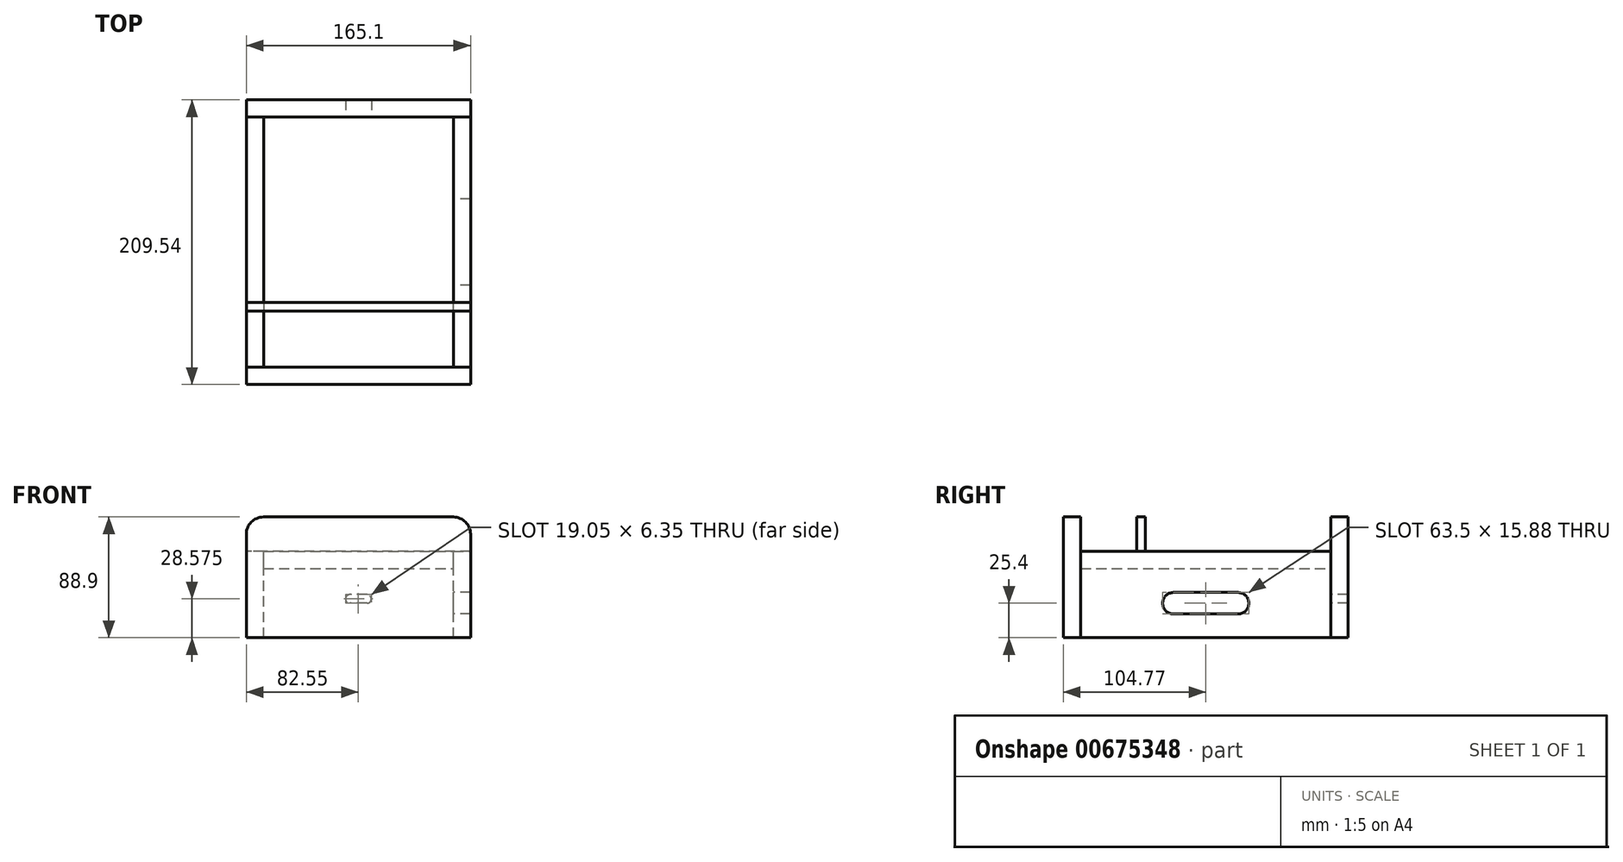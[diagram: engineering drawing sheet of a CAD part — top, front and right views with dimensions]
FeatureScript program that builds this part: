
annotation { "Feature Type Name" : "Feature", "Feature Type Description" : "" }
export const myFeature = defineFeature(function(context is Context, id is Id, definition is map)
    precondition{}
    {
        {
            var Q0;
            Q0=qCreatedBy(makeId("Top.planeOp"),FACE);
            var sketch = newSketch(context, id + "F0", { "sketchPlane" : qUnion([Q0])});
            skLineSegment(sketch, "E0.bottom", {"start": v(69.85, -92.07) * mm, "end": v(-69.85, -92.08) * mm, "construction": true});
            skLineSegment(sketch, "E0.top", {"start": v(69.85, 92.08) * mm, "end": v(-69.85, 92.07) * mm, "construction": true});
            skLineSegment(sketch, "E0.left", {"start": v(69.85, -92.07) * mm, "end": v(69.85, 92.08) * mm, "construction": true});
            skLineSegment(sketch, "E0.right", {"start": v(-69.85, -92.08) * mm, "end": v(-69.85, 92.07) * mm, "construction": true});
            skPoint(sketch, "E0.middle", {"position": v(0, 0) * mm});
            skLineSegment(sketch, "E1.bottom", {"start": v(-69.85, -92.08) * mm, "end": v(-82.55, -92.08) * mm});
            skLineSegment(sketch, "E1.top", {"start": v(-69.85, 92.07) * mm, "end": v(-82.55, 92.07) * mm});
            skLineSegment(sketch, "E1.left", {"start": v(-69.85, -92.08) * mm, "end": v(-69.85, 92.07) * mm});
            skLineSegment(sketch, "E1.right", {"start": v(-82.55, -92.08) * mm, "end": v(-82.55, 92.07) * mm});
            skLineSegment(sketch, "E2.bottom", {"start": v(69.85, -92.07) * mm, "end": v(82.55, -92.07) * mm});
            skLineSegment(sketch, "E2.top", {"start": v(69.85, 92.08) * mm, "end": v(82.55, 92.08) * mm});
            skLineSegment(sketch, "E2.left", {"start": v(69.85, -92.07) * mm, "end": v(69.85, 92.08) * mm});
            skLineSegment(sketch, "E2.right", {"start": v(82.55, -92.07) * mm, "end": v(82.55, 92.08) * mm});
            skLineSegment(sketch, "E3.bottom", {"start": v(82.55, 92.08) * mm, "end": v(-82.55, 92.07) * mm});
            skLineSegment(sketch, "E3.top", {"start": v(82.55, 104.78) * mm, "end": v(-82.55, 104.77) * mm});
            skLineSegment(sketch, "E3.left", {"start": v(82.55, 92.08) * mm, "end": v(82.55, 104.78) * mm});
            skLineSegment(sketch, "E3.right", {"start": v(-82.55, 92.07) * mm, "end": v(-82.55, 104.77) * mm});
            skLineSegment(sketch, "E4.bottom", {"start": v(-82.55, -92.08) * mm, "end": v(82.55, -92.08) * mm});
            skLineSegment(sketch, "E4.top", {"start": v(-82.55, -104.78) * mm, "end": v(82.55, -104.78) * mm});
            skLineSegment(sketch, "E4.left", {"start": v(-82.55, -92.08) * mm, "end": v(-82.55, -104.78) * mm});
            skLineSegment(sketch, "E4.right", {"start": v(82.55, -92.07) * mm, "end": v(82.55, -104.78) * mm});
            skSolve(sketch);
        }
        {
            var Q0;
            {var subQ0=sQuery(id+"F0.wireOp",EDGE,"E2.left");Q0=makeQuery(id+"F0.imprint","IMPRINT",FACE,{"disambiguationData":[TD([[makeQuery(id+"F0.imprint","IMPRINT",EDGE,{"derivedFrom":subQ0}),-1.0]])]});}
            var Q1;
            {var subQ0=sQuery(id+"F0.wireOp",EDGE,"E1.left");Q1=makeQuery(id+"F0.imprint","IMPRINT",FACE,{"disambiguationData":[TD([[makeQuery(id+"F0.imprint","IMPRINT",EDGE,{"derivedFrom":subQ0}),1.0]])]});}
            extrude(context, id + "F1", {"entities" : qUnion([Q0, Q1]), "oppositeDirection" : true, "depth" : 63.5 * mm, "offsetDistance" : 25.4 * mm});
        }
        {
            var Q0;
            Q0=makeQuery(id+"F0.imprint","IMPRINT",FACE,{"disambiguationData":[TD([[makeQuery(id+"F0.imprint","IMPRINT",EDGE,{"derivedFrom":sQuery(id+"F0.wireOp",EDGE,"E4.top")}),1.0]])]});
            var Q1;
            Q1=makeQuery(id+"F0.imprint","IMPRINT",FACE,{"disambiguationData":[TD([[makeQuery(id+"F0.imprint","IMPRINT",EDGE,{"derivedFrom":sQuery(id+"F0.wireOp",EDGE,"E3.top")}),1.0]])]});
            var Q2;
            Q2=makeQuery(id+"F1.opExtrude","CAP_FACE",FACE,{"disambiguationData":[OSD([sQuery(id+"F0.wireOp",EDGE,"E2.left"),sQuery(id+"F0.wireOp",EDGE,"E2.right"),sQuery(id+"F0.wireOp",EDGE,"E3.bottom"),sQuery(id+"F0.wireOp",EDGE,"E4.bottom")])],"isStart":false});
            extrude(context, id + "F2", {"entities" : qUnion([Q0, Q1]), "depth" : 25.4 * mm, "offsetDistance" : 25.4 * mm, "hasSecondDirection" : true, "secondDirectionBound" : SecondDirectionBoundingType.UP_TO_SURFACE, "secondDirectionOppositeDirection" : true, "secondDirectionDepth" : 50.8 * mm, "secondDirectionBoundEntityFace" : qUnion([Q2])});
        }
        {
            var Q0;
            Q0=qCreatedBy(makeId("Top.planeOp"),FACE);
            var sketch = newSketch(context, id + "F3", { "sketchPlane" : qUnion([Q0])});
            skLineSegment(sketch, "E5.0.0", {"start": v(69.85, -92.08) * mm, "end": v(69.85, 92.08) * mm});
            skLineSegment(sketch, "E5.0.1", {"start": v(69.85, 92.08) * mm, "end": v(-69.85, 92.07) * mm});
            skLineSegment(sketch, "E5.0.2", {"start": v(-69.85, 92.07) * mm, "end": v(-69.85, -92.08) * mm});
            skLineSegment(sketch, "E5.0.3", {"start": v(-69.85, -92.08) * mm, "end": v(69.85, -92.08) * mm});
            skSolve(sketch);
        }
        {
            var Q0;
            Q0 = qSketchRegion(id + "F3", true);
            extrude(context, id + "F4", {"entities" : qUnion([Q0]), "oppositeDirection" : true, "depth" : 12.7 * mm, "offsetDistance" : 25.4 * mm});
        }
        {
            var Q0;
            Q0=qCreatedBy(makeId("Right.planeOp"),FACE);
            var sketch = newSketch(context, id + "F5", { "sketchPlane" : qUnion([Q0])});
            skLineSegment(sketch, "E6", {"start": v(-23.81, -38.1) * mm, "end": v(23.81, -38.1) * mm, "construction": true});
            skArc(sketch, "E7.0.startCap", {"start": v(-23.81, -46.04) * mm, "mid": v(-31.75, -38.1) * mm, "end": v(-23.81, -30.16) * mm});
            skArc(sketch, "E7.0.endCap", {"start": v(23.81, -30.16) * mm, "mid": v(31.75, -38.1) * mm, "end": v(23.81, -46.04) * mm});
            skLineSegment(sketch, "E7.0.left", {"start": v(-23.81, -30.16) * mm, "end": v(23.81, -30.16) * mm});
            skLineSegment(sketch, "E7.0.right", {"start": v(-23.81, -46.04) * mm, "end": v(23.81, -46.04) * mm});
            skSolve(sketch);
        }
        {
            var Q0;
            Q0 = qSketchRegion(id + "F5", true);
            extrude(context, id + "F6", {"entities" : qUnion([Q0]), "operationType" : NewBodyOperationType.REMOVE, "endBound" : BoundingType.THROUGH_ALL, "depth" : 25.4 * mm, "offsetDistance" : 25.4 * mm});
        }
        {
            var Q0;
            Q0=qCreatedBy(makeId("Top.planeOp"),FACE);
            var sketch = newSketch(context, id + "F7", { "sketchPlane" : qUnion([Q0])});
            skLineSegment(sketch, "E8.bottom", {"start": v(82.55, -50.8) * mm, "end": v(-82.55, -50.8) * mm});
            skLineSegment(sketch, "E8.top", {"start": v(82.55, -44.45) * mm, "end": v(-82.55, -44.45) * mm});
            skLineSegment(sketch, "E8.left", {"start": v(82.55, -50.8) * mm, "end": v(82.55, -44.45) * mm});
            skLineSegment(sketch, "E8.right", {"start": v(-82.55, -50.8) * mm, "end": v(-82.55, -44.45) * mm});
            skPoint(sketch, "E8.middle", {"position": v(0, -47.62) * mm});
            skSolve(sketch);
        }
        {
            var Q0;
            Q0 = qSketchRegion(id + "F7", true);
            extrude(context, id + "F8", {"entities" : qUnion([Q0]), "depth" : 25.4 * mm, "offsetDistance" : 25.4 * mm});
        }
        {
            var Q0;
            Q0=makeQuery(id+"F2.opExtrude","CAP_EDGE",EDGE,{"disambiguationData":[OSD([sQuery(id+"F0.wireOp",EDGE,"E3.right")])],"isStart":false});
            var Q1;
            Q1=makeQuery(id+"F2.opExtrude","CAP_EDGE",EDGE,{"disambiguationData":[OSD([sQuery(id+"F0.wireOp",EDGE,"E3.left")])],"isStart":false});
            var Q2;
            Q2=makeQuery(id+"F2.opExtrude","CAP_EDGE",EDGE,{"disambiguationData":[OSD([sQuery(id+"F0.wireOp",EDGE,"E4.left")])],"isStart":false});
            var Q3;
            Q3=makeQuery(id+"F2.opExtrude","CAP_EDGE",EDGE,{"disambiguationData":[OSD([sQuery(id+"F0.wireOp",EDGE,"E4.right")])],"isStart":false});
            var Q4;
            Q4=makeQuery(id+"F8.opExtrude","CAP_EDGE",EDGE,{"disambiguationData":[OSD([sQuery(id+"F7.wireOp",EDGE,"E8.left")])],"isStart":false});
            var Q5;
            Q5=makeQuery(id+"F8.opExtrude","CAP_EDGE",EDGE,{"disambiguationData":[OSD([sQuery(id+"F7.wireOp",EDGE,"E8.right")])],"isStart":false});
            fillet(context, id + "F9", {"entities" : qUnion([Q0, Q1, Q2, Q3, Q4, Q5]), "radius" : 12.7 * mm, "tangentPropagation" : true, "allowEdgeOverflow" : false});
        }
        {
            var Q0;
            Q0=qCreatedBy(makeId("Front.planeOp"),FACE);
            var sketch = newSketch(context, id + "F10", { "sketchPlane" : qUnion([Q0])});
            skLineSegment(sketch, "E9", {"start": v(-6.35, -34.93) * mm, "end": v(6.35, -34.93) * mm, "construction": true});
            skPoint(sketch, "E10", {"position": v(0, -34.93) * mm});
            skArc(sketch, "E11.0.startCap", {"start": v(-6.35, -38.1) * mm, "mid": v(-9.52, -34.93) * mm, "end": v(-6.35, -31.75) * mm});
            skArc(sketch, "E11.0.endCap", {"start": v(6.35, -31.75) * mm, "mid": v(9.52, -34.93) * mm, "end": v(6.35, -38.1) * mm});
            skLineSegment(sketch, "E11.0.left", {"start": v(-6.35, -31.75) * mm, "end": v(6.35, -31.75) * mm});
            skLineSegment(sketch, "E11.0.right", {"start": v(-6.35, -38.1) * mm, "end": v(6.35, -38.1) * mm});
            skSolve(sketch);
        }
        {
            var Q0;
            Q0 = qSketchRegion(id + "F10", true);
            extrude(context, id + "F11", {"entities" : qUnion([Q0]), "operationType" : NewBodyOperationType.REMOVE, "endBound" : BoundingType.THROUGH_ALL, "oppositeDirection" : true, "depth" : 25.4 * mm, "offsetDistance" : 25.4 * mm});
        }
    });
